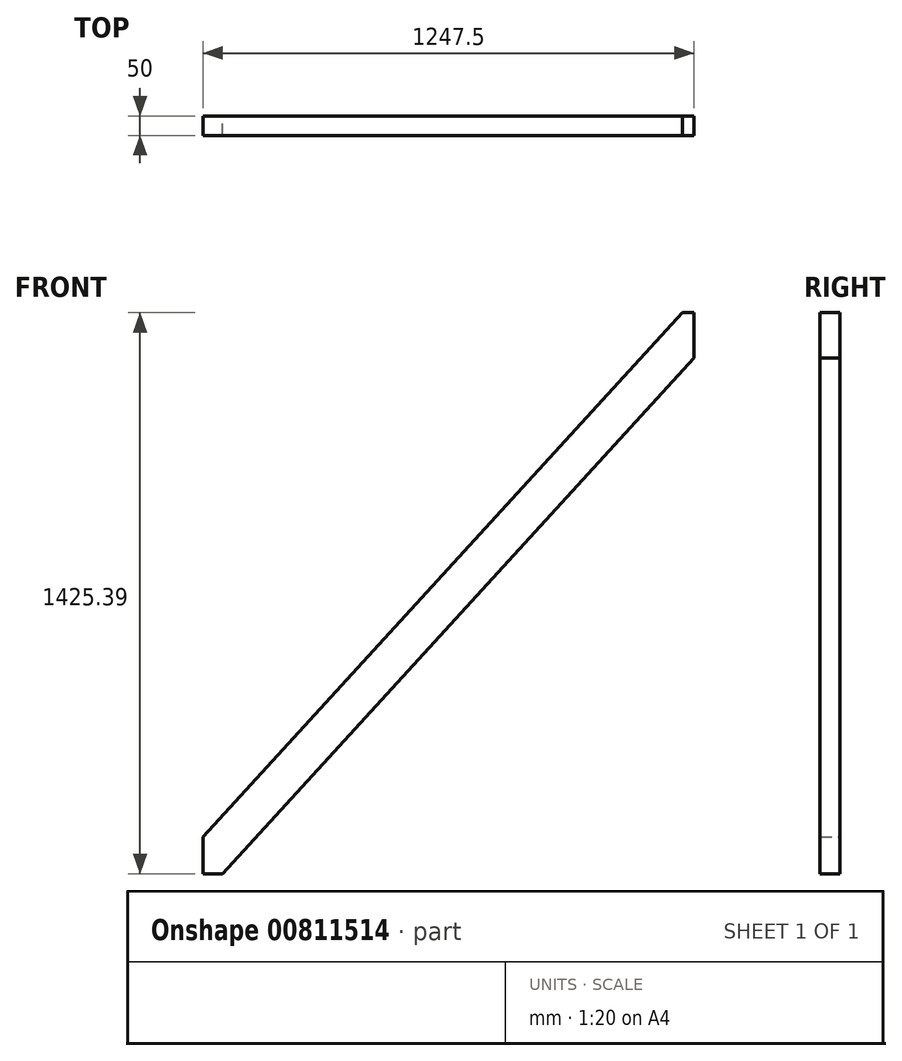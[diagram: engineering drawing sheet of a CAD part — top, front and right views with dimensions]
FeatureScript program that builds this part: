
annotation { "Feature Type Name" : "Feature", "Feature Type Description" : "" }
export const myFeature = defineFeature(function(context is Context, id is Id, definition is map)
    precondition{}
    {
        {
            var Q0;
            Q0=qCreatedBy(makeId("Front.planeOp"),FACE);
            var sketch = newSketch(context, id + "F0", { "sketchPlane" : qUnion([Q0])});
            skLineSegment(sketch, "E0", {"start": v(-1197.5, 0) * mm, "end": v(1197.5, 0) * mm, "construction": true});
            skLineSegment(sketch, "E1", {"start": v(1197.5, 0) * mm, "end": v(0, 1310) * mm, "construction": true});
            skLineSegment(sketch, "E2", {"start": v(0, 1310) * mm, "end": v(-1197.5, 0) * mm});
            skLineSegment(sketch, "E3", {"start": v(0, 1310) * mm, "end": v(-73.8, 1377.47) * mm});
            skLineSegment(sketch, "E4", {"start": v(-1197.5, 0) * mm, "end": v(-1247.5, 0) * mm});
            skLineSegment(sketch, "E5", {"start": v(-1247.5, 93.52) * mm, "end": v(-73.8, 1377.47) * mm});
            skLineSegment(sketch, "E6", {"start": v(-1247.5, 0) * mm, "end": v(-1247.5, 93.52) * mm});
            skLineSegment(sketch, "E7", {"start": v(0, 1310) * mm, "end": v(0, 1458.21) * mm});
            skLineSegment(sketch, "E8", {"start": v(-73.8, 1377.47) * mm, "end": v(0, 1458.21) * mm});
            skLineSegment(sketch, "E9", {"start": v(-30, 1425.4) * mm, "end": v(0, 1425.4) * mm});
            skSolve(sketch);
        }
        {
            var Q0;
            Q0=makeQuery(id+"F0.imprint","IMPRINT",FACE,{"disambiguationData":[TD([[makeQuery(id+"F0.imprint","IMPRINT",EDGE,{"derivedFrom":sQuery(id+"F0.wireOp",EDGE,"E2")}),-1.0]])]});
            var Q1;
            Q1=makeQuery(id+"F0.imprint","IMPRINT",FACE,{"disambiguationData":[TD([[makeQuery(id+"F0.imprint","IMPRINT",EDGE,{"derivedFrom":sQuery(id+"F0.wireOp",EDGE,"E3")}),-1.0]])]});
            extrude(context, id + "F1", {"entities" : qUnion([Q0, Q1]), "depth" : 50 * mm, "offsetDistance" : 25 * mm});
        }
    });
